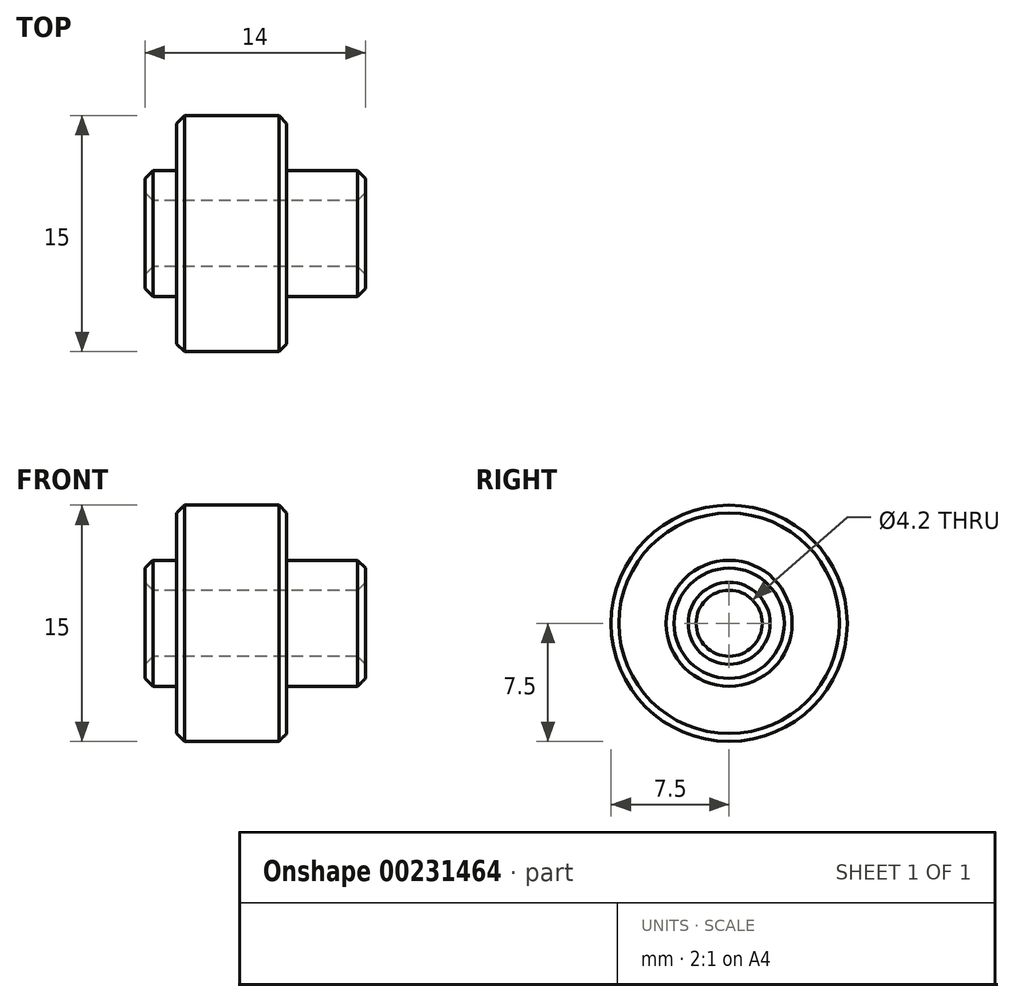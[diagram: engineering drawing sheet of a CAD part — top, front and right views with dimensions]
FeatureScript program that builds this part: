
annotation { "Feature Type Name" : "Feature", "Feature Type Description" : "" }
export const myFeature = defineFeature(function(context is Context, id is Id, definition is map)
    precondition{}
    {
        {
            var Q0;
            Q0=qCreatedBy(makeId("Front.planeOp"),FACE);
            var sketch = newSketch(context, id + "F0", { "sketchPlane" : qUnion([Q0])});
            skLineSegment(sketch, "E0", {"start": v(0, 2.1) * mm, "end": v(0, 4) * mm});
            skLineSegment(sketch, "E1", {"start": v(0, 4) * mm, "end": v(2, 4) * mm});
            skLineSegment(sketch, "E2", {"start": v(2, 4) * mm, "end": v(2, 7.5) * mm});
            skLineSegment(sketch, "E3", {"start": v(2, 7.5) * mm, "end": v(9, 7.5) * mm});
            skLineSegment(sketch, "E4", {"start": v(9, 7.5) * mm, "end": v(9, 4) * mm});
            skLineSegment(sketch, "E5", {"start": v(9, 4) * mm, "end": v(14, 4) * mm});
            skLineSegment(sketch, "E6", {"start": v(14, 4) * mm, "end": v(14, 2.1) * mm});
            skLineSegment(sketch, "E7", {"start": v(14, 2.1) * mm, "end": v(0, 2.1) * mm});
            skLineSegment(sketch, "E8", {"start": v(-6.55, 0) * mm, "end": v(25.4, 0) * mm, "construction": true});
            skSolve(sketch);
        }
        {
            var Q0;
            Q0=makeQuery(id+"F0.imprint","IMPRINT",FACE,{"disambiguationData":[TD([[makeQuery(id+"F0.imprint","IMPRINT",EDGE,{"derivedFrom":sQuery(id+"F0.wireOp",EDGE,"E0")}),-1.0]])]});
            var Q1;
            Q1=sQuery(id+"F0.wireOp",EDGE,"E8");
            revolve(context, id + "F1", {"entities" : qUnion([Q0]), "axis" : qUnion([Q1]), "revolveType" : RevolveType.FULL});
        }
        {
            var Q0;
            Q0=makeQuery(id+"F1.opRevolve","SWEPT_FACE",FACE,{"disambiguationData":[OSD([sQuery(id+"F0.wireOp",EDGE,"E3")])]});
            var Q1;
            Q1=makeQuery(id+"F1.opRevolve","SWEPT_FACE",FACE,{"disambiguationData":[OSD([sQuery(id+"F0.wireOp",EDGE,"E7")])]});
            var Q2;
            Q2=makeQuery(id+"F1.opRevolve","SWEPT_EDGE",EDGE,{"disambiguationData":[OSD([sQuery(id+"F0.wireOp",EDGE,"E5"),sQuery(id+"F0.wireOp",EDGE,"E6")])]});
            var Q3;
            Q3=makeQuery(id+"F1.opRevolve","SWEPT_EDGE",EDGE,{"disambiguationData":[OSD([sQuery(id+"F0.wireOp",EDGE,"E0"),sQuery(id+"F0.wireOp",EDGE,"E1")])]});
            chamfer(context, id + "F2", {"entities" : qUnion([Q0, Q1, Q2, Q3]), "width" : 0.5 * mm, "tangentPropagation" : true});
        }
    });
